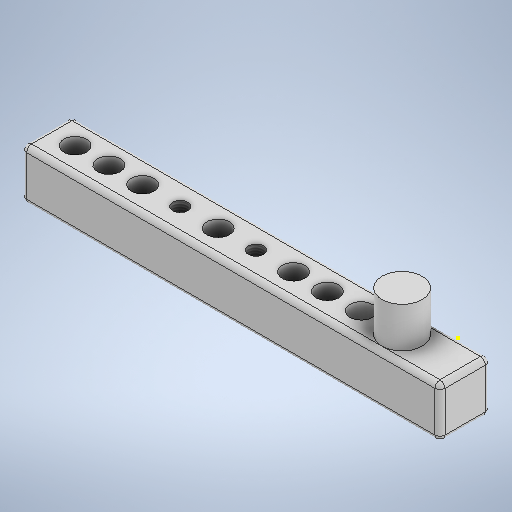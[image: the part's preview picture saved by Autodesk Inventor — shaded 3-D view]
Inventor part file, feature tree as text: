
AUTODESK INVENTOR PART (.ipt)
format: ipt  version: 2025.2 (Build 292293000, 293)  size: 443,904 bytes
history: native  units: in
note: dims shown in document units (in); Inventor stores cm internally (conversion verified against a paired STEP export)
features: sketch x20, extrude x17, thread x4, fillet x3
ambient origin geometry x8: Origin, YZ Plane, XZ Plane, XY Plane, X Axis, Y Axis, Z Axis, Center Point
bodies: Solid1 (feature_tree)
feature tree (44):
  extrude  "Extrusion1"  Depth=0.3937in
  sketch  "Sketch2"  dims[d8=0.1181in d9=0.1181in]
  extrude  "Extrusion2"  Depth=0.3937in
  extrude  "Extrusion3"  Depth=0.1181in
  extrude  "Extrusion4"  Depth=0.3937in TaperAngle=0.0deg
  extrude  "Extrusion5"  Depth=0.3937in
  thread  "Thread1"  [1 undecoded]
  thread  "Thread2"  [1 undecoded]
  extrude  "Extrusion6"  Depth=0.3937in TaperAngle=0.0deg
  extrude  "Extrusion7"  Depth=0.3937in TaperAngle=0.0deg
  extrude  "Extrusion8"  Depth=0.0394in
  sketch  "Sketch7"  dims[d61=0.5906in d62=0.5906in]
  fillet  "Fillet3"  Radius=0.0394in
  fillet  "Fillet4"  Radius=0.1969in
  sketch  "Sketch8"  dims[d63=0.1181in d64=0.1181in]
  extrude  "Extrusion9"  Depth=0.3937in
  extrude  "Extrusion10"  Depth=0.3937in TaperAngle=0.0deg
  extrude  "Extrusion11"  Depth=0.5906in
  extrude  "Extrusion12"  Depth=0.1181in
  extrude  "Extrusion13"  Depth=0.3937in
  extrude  "Extrusion14"  Depth=0.1457in
  thread  "Thread3"  [1 undecoded]
  thread  "Thread4"  [1 undecoded]
  fillet  "Fillet5"  Radius=0.3937in
  extrude  "Extrusion15"  Depth=0.3937in TaperAngle=0.0deg
  sketch  "Sketch16"  dims[d106=0.3937in d107=0.0in d108=0.315in d109=0.3937in d110=0.0in d111=0.315in d112=0.0in]
  extrude  "Extrusion16"  Depth=0.3937in TaperAngle=0.0deg
  extrude  "Extrusion17"  Depth=0.0394in
  sketch  "Sketch1"  dims[d0=6.6929in d1=0.3937in]
  sketch  "Sketch3"  dims[d14=0.3937in d15=0.0in d18=2.7559in d20=0.3937in d21=0.3937in d23=0.3937in d30=2.3622in d32=0.3937in d33=0.3937in d35=0.3937in d37=0.3937in d38=0.0in]
  sketch  "Sketch Rectangular Pattern1"  dims[d2=0.3937in d3=0.0in d4=0.0866in]
  sketch  "Sketch Rectangular Pattern2"  dims[d10=0.3937in d11=0.0in d12=0.3937in d13=0.0in]
  sketch  "Sketch4"  dims[d39=0.3937in d40=0.0in d41=0.3937in d42=0.0in]
  sketch  "Sketch5"  dims[d49=0.3937in d50=0.0in d51=0.0394in d52=0.0394in d53=0.1969in]
  sketch  "Sketch6"  dims[d57=0.3937in d58=0.0in d59=0.3937in d60=0.0in]
  sketch  "Sketch9"  dims[d65=0.3937in d66=0.0in d67=0.1772in]
  sketch  "Sketch10"  dims[d68=0.1457in d69=0.1457in d71=0.1772in d73=0.1772in]
  sketch  "Sketch11"  dims[d81=1.1811in d83=0.2638in d84=0.3937in d86=0.3937in]
  sketch  "Sketch12"  dims[d88=1.1811in d90=0.2638in d91=0.3937in d93=0.3937in d95=0.3937in d96=0.0in]
  sketch  "Sketch13"  dims[d97=0.1772in d98=0.3937in d99=0.0in]
  sketch  "Sketch Rectangular Pattern4"  dims[d44=0.3937in d45=0.0in d46=0.3937in d47=0.0in]
  sketch  "Sketch Rectangular Pattern5"  dims[d54=0.3937in d55=0.0in d56=0.1969in]
  sketch  "Sketch14"  dims[d100=0.3937in d101=0.0in d102=0.3937in d103=0.0in]
  sketch  "Sketch15"  dims[d104=0.0394in d105=0.2165in]
note: 4 required parameter values undecoded (feature->parameter linkage not recoverable at this tier; creation-order binding heuristic only, values carry confidence <= 0.55)
